# Revit family: Echo Eliminator - Acoustical Backer
name_source: partatom
category: Generic Models
revit_build: Autodesk Revit 2016 (Build: 20150220_1215(x64)
units: mm (PartAtom-declared; Revit-internal decimal feet)

## family parameters
Always vertical = No
Can host rebar = No
Cut with Voids When Loaded = No
Part Type = Normal
Room Calculation Point = No
Round Connector Dimension = Use Diameter
Shared = No
Work Plane-Based = Yes

## types (4) — shared parameters
A = 0' - 0"
Default Elevation = 4' - 0"
Finish = Echo Eliminator - Acoustical Backer - Marble Blue
Length = 4' - 0"
Manufacturer = Acoustical Surfaces, Inc.
Material = Echo Eliminator - Acoustical Backer
URL = https://www.acousticalsurfaces.com
Width = 4' - 0"

## per-type parameters (varying)
| type | Thickness |
| 2 INCH THICK - 48 inch wdith | 0' - 2" |
| 1.5 INCH THICK - 48 inch wdith 2 | 0' - 1 1/2" |
| 1 INCH THICK - 48 inch wdith | 0' - 1" |
| HALF INCH THICK - 48 inch wdith | 0' - 0 1/2" |

## geometry (parser evidence)
native form markers: Sweep x4
no freeform markers — native parametric forms only
